# Revit family: Shower-Shower_Column_Kit-KOHLER-Aleo-K-97825T_
name_source: partatom
category: Plumbing Fixtures
units: mm (PartAtom-declared; Revit-internal decimal feet)

## family parameters
Cut with Voids When Loaded = No
Host = Face
OmniClass Number = 23.31.17.00
OmniClass Title = Showers
Part Type = Normal
Room Calculation Point = No
Round Connector Dimension = Use Diameter
Shared = No

## types (3) — shared parameters
ADA Compliant = No
Assembly Code = D2010700
CW Connection = Yes
Cold Water Inlet = Cold Water Inlet
Date Modified = 03/29/2023
Default Elevation = 42"
Drain Included = No
Finish = Kohler-Metal-CP-Polished_Chrome
Flow Rate = 3 GPM
HW Connection = Yes
Handle Clearance = 3 11/16"
Height = 51 1/8"
Hot Water Inlet = Hot Water Inlet
Manufacturer = Kohler Co.
Master Format 2014 = 22 42 23
Master Format 2014 Name = Residential Showers
Material = Premium Metal Construction
Pressure = 80.00 psi
Product Documentation Link = https://files.kohler.com.cn
Product Name = Aleo
Secondary Finish = Kohler-Plastic-0-White
Spout Reach = 7 7/8"
URL = http://www.kohler.com.cn
Vent Connection = No
Waste Connection = No
Waste Water Outlet = Waste Water Outlet
WaterSense Certified = No
Width = 5 15/16"

## per-type parameters (varying)
| type | 4 | B4 | Description | Distance 1 | Distance 2 | Length | Model | Product Page URL | Type |
| 4, CP-Polished Chrome | Yes | No | Three Outlet Shower Column Hard Pipe Connection | 4 5/16" | 8" | 23 3/8" | K-97825T-4-CP | https://www.kohler.com.cn | 1 |
| 4E2, CP-Polished Chrome | Yes | No | Three Outlet Shower Column Hard Pipe Connection | 4 5/16" | 8" | 23 3/8" | K-97825T-4E2-CP |  | 2 |
| B4, CP-Polished Chrome | No | Yes | Triple Water Shower Column – Rigid Tube Connection | 4 15/16" | 10" | 24 3/8" | K-97825T-B4-CP | https://www.kohler.com.cn | 3 |

## geometry (parser evidence)
native form markers: Sweep x6
no freeform markers — native parametric forms only
